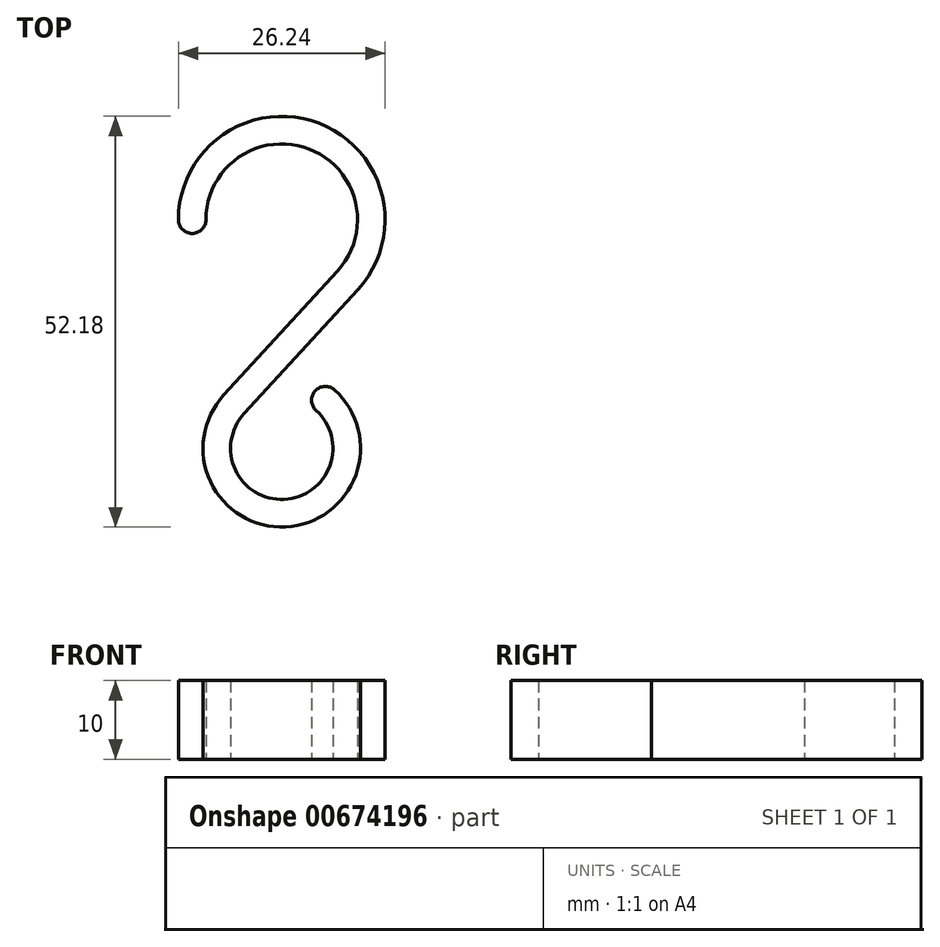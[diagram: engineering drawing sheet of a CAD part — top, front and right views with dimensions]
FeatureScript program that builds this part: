
annotation { "Feature Type Name" : "Feature", "Feature Type Description" : "" }
export const myFeature = defineFeature(function(context is Context, id is Id, definition is map)
    precondition{}
    {
        {
            var Q0;
            Q0=qCreatedBy(makeId("Top.planeOp"),FACE);
            var sketch = newSketch(context, id + "F0", { "sketchPlane" : qUnion([Q0])});
            skArc(sketch, "E0", {"start": v(7.1, -6.5) * mm, "mid": v(3.49, 8.97) * mm, "end": v(-9.63, 0) * mm});
            skArc(sketch, "E1", {"start": v(-4.8, -24.66) * mm, "mid": v(0.3, -35.54) * mm, "end": v(4.36, -24.23) * mm});
            skArc(sketch, "E2", {"start": v(9.68, -8.87) * mm, "mid": v(4.76, 12.23) * mm, "end": v(-13.12, 0) * mm});
            skArc(sketch, "E3", {"start": v(-7.37, -22.3) * mm, "mid": v(0.47, -39.04) * mm, "end": v(6.71, -21.64) * mm});
            skLineSegment(sketch, "E4", {"start": v(7.1, -6.5) * mm, "end": v(-7.37, -22.3) * mm});
            skLineSegment(sketch, "E5", {"start": v(9.68, -8.87) * mm, "end": v(-4.8, -24.66) * mm});
            skArc(sketch, "E6", {"start": v(-13.12, 0) * mm, "mid": v(-11.38, -1.75) * mm, "end": v(-9.62, 0) * mm});
            skArc(sketch, "E7", {"start": v(6.71, -21.64) * mm, "mid": v(4.24, -21.76) * mm, "end": v(4.36, -24.23) * mm});
            skPoint(sketch, "E8.center.orphan", {"position": v(8.25, -29.05) * mm});
            skPoint(sketch, "E8.end.orphan", {"position": v(6.5, -29.05) * mm});
            skPoint(sketch, "E8.start.orphan", {"position": v(10, -29.05) * mm});
            skSolve(sketch);
        }
        {
            var Q0;
            Q0=makeQuery(id+"F0.imprint","IMPRINT",FACE,{"disambiguationData":[TD([[makeQuery(id+"F0.imprint","IMPRINT",EDGE,{"derivedFrom":sQuery(id+"F0.wireOp",EDGE,"E0")}),-1.0]])]});
            extrude(context, id + "F1", {"entities" : qUnion([Q0]), "depth" : 10 * mm, "offsetDistance" : 25 * mm});
        }
    });
